# Revit family: Rundstahlbügel, Ø 21,3-219,1
name_source: partatom
category: HLS-Bauteile
revit_build: Autodesk Revit 2017 (Build: 20190507_1515(x64)
units: mm (PartAtom-declared; Revit-internal decimal feet)

## family parameters
Arbeitsebenenbasiert = Ja
Beim Laden mit Abzugskörper schneiden = Nein
Bemaßung runder Anschluss = Durchmesser verwenden
Gemeinsam genutzt = Ja
Immer vertikal = Nein
Raumberechnungspunkt = Nein
Teiletyp = Normal

## types (15) — shared parameters
Fabrikat = MEFA
Firma = MEFA Befestigungs- und Montagesysteme GmbH
Vorgabe-Ansicht = 1219 mm
zero-valued in all types: Nennweite DN Rohr, max. Profilhöhe

## per-type parameters (varying)
| type | A | Achsabstand | Artikelnummer | B | EAN | Gewicht | Gewicht pro Bauteil | Gewinde | H | Höhe | Kurztext1 | Kurztext2 | L1 | Länge Gewinde | M | Material | Materialname | Mengeneinheit | Oberflaeche | Rohraußendurchmesser | Rohraußendurchmesser Zoll | d2 | vpe |
| Rundstahlbügel, M 8, Ø 21,3 | 30 mm  [stored 0.0984252 ft] | 30 mm | 050702201 | 70 mm  [stored 0.229659 ft] |  | 0.00 kg | 0.00 kg | M8 | 85 mm  [stored 0.278871 ft] | 80 mm | Rundstahlbügel |  | 4 mm  [stored 0.0131234 ft] | 65 mm  [stored 0.213255 ft] | 8 mm  [stored 0.0262467 ft] |  |  |  |  | 21 mm | 1/2 Zoll | 7 mm  [stored 0.0229659 ft] |  |
| Rundstahlbügel, M 8, Ø 26,9 | 35 mm  [stored 0.114829 ft] | 35 mm | 050702801 | 70 mm  [stored 0.229659 ft] |  | 0.00 kg | 0.00 kg | M8 | 85 mm  [stored 0.278871 ft] | 80 mm |  |  | 1 mm  [stored 0.00328084 ft] | 65 mm  [stored 0.213255 ft] | 8 mm  [stored 0.0262467 ft] |  |  |  |  | 27 mm | 3/4 Zoll | 7 mm  [stored 0.0229659 ft] |  |
| Rundstahlbügel, M 8, Ø 33,7 | 35 mm  [stored 0.114829 ft] | 42 mm | 050703501 | 70 mm  [stored 0.229659 ft] |  | 0.00 kg | 0.00 kg | M8 | 95 mm | 90 mm |  |  | 11 mm | 65 mm  [stored 0.213255 ft] | 8 mm  [stored 0.0262467 ft] |  |  |  |  | 34 mm | 1 Zoll | 7 mm  [stored 0.0229659 ft] |  |
| Rundstahlbügel, M 8, Ø 42,4 | 51 mm | 51 mm | 050704201 | 75 mm |  | 0.00 kg | 0.00 kg | M8 | 105 mm  [stored 0.344488 ft] | 100 mm |  |  | 8 mm  [stored 0.0262467 ft] | 70 mm  [stored 0.229659 ft] | 8 mm  [stored 0.0262467 ft] |  |  |  |  | 42 mm | 1 1/4 Zoll | 7 mm  [stored 0.0229659 ft] |  |
| Rundstahlbügel, M 8, Ø 48,3 | 57 mm  [stored 0.187008 ft] | 57 mm | 050704801 | 75 mm |  | 0.00 kg | 0.00 kg | M8 | 110 mm  [stored 0.360892 ft] | 105 mm |  |  | 10 mm  [stored 0.0328084 ft] | 70 mm  [stored 0.229659 ft] | 8 mm  [stored 0.0262467 ft] |  |  |  |  | 48 mm | 1 1/2 Zoll | 7 mm  [stored 0.0229659 ft] |  |
| Rundstahlbügel, M10, Ø 60,3 | 71 mm  [stored 0.23294 ft] | 71 mm | 050706001 | 75 mm |  | 0.00 kg | 0.00 kg | M10 | 125 mm | 120 mm |  |  | 19 mm | 70 mm  [stored 0.229659 ft] | 10 mm  [stored 0.0328084 ft] |  |  |  |  | 60 mm | 2 Zoll | 9 mm |  |
| Rundstahlbügel, M10, Ø 76,1 | 87 mm  [stored 0.285433 ft] | 87 mm | 050707601 | 75 mm |  | 0.00 kg | 0.00 kg | M10 | 140 mm | 135 mm |  |  | 26 mm | 70 mm  [stored 0.229659 ft] | 10 mm  [stored 0.0328084 ft] |  |  |  |  | 76 mm | 2 1/2 Zoll | 9 mm |  |
| Rundstahlbügel, M10, Ø 88,9 | 100 mm  [stored 0.328084 ft] | 100 mm | 050708901 | 75 mm |  | 0.00 kg | 0.00 kg | M10 | 155 mm | 150 mm |  |  | 34 mm | 70 mm  [stored 0.229659 ft] | 10 mm  [stored 0.0328084 ft] |  |  |  |  | 89 mm | 3 Zoll | 9 mm |  |
| Rundstahlbügel, M12, Ø108 | 121 mm | 121 mm | 050710801 | 95 mm |  | 0.00 kg | 0.00 kg | M12 | 195 mm | 190 mm |  |  | 45 mm | 90 mm  [stored 0.295276 ft] | 12 mm  [stored 0.0393701 ft] |  |  |  |  | 108 mm  [stored 0.354331 ft] |  | 11 mm |  |
| Rundstahlbügel, M12, Ø114,3 | 126 mm | 126 mm | 050711401 | 95 mm |  | 0.00 kg | 0.00 kg | M12 | 200 mm | 195 mm |  |  | 47 mm | 90 mm  [stored 0.295276 ft] | 12 mm  [stored 0.0393701 ft] |  |  |  |  | 114 mm | 4 Zoll | 11 mm |  |
| Rundstahlbügel, M12, Ø133 | 146 mm | 146 mm | 050713301 | 95 mm |  | 0.00 kg | 0.00 kg | M12 | 220 mm | 215 mm |  |  | 57 mm  [stored 0.187008 ft] | 90 mm  [stored 0.295276 ft] | 12 mm  [stored 0.0393701 ft] |  |  |  |  | 133 mm |  | 11 mm |  |
| Rundstahlbügel, M12, Ø139,7 | 152 mm | 152 mm | 050714001 | 95 mm |  | 0.00 kg | 0.00 kg | M12 | 225 mm | 220 mm |  |  | 59 mm | 90 mm  [stored 0.295276 ft] | 12 mm  [stored 0.0393701 ft] |  |  |  |  | 140 mm | 5 Zoll | 11 mm |  |
| Rundstahlbügel, M12, Ø159 | 172 mm | 172 mm | 050715901 | 95 mm |  | 0.00 kg | 0.00 kg | M12 | 245 mm | 240 mm |  |  | 69 mm | 90 mm  [stored 0.295276 ft] | 12 mm  [stored 0.0393701 ft] |  |  |  |  | 159 mm |  | 11 mm |  |
| Rundstahlbügel, M12, Ø168,3 | 180 mm | 180 mm | 050716801 | 95 mm |  | 0.00 kg | 0.00 kg | M12 | 255 mm | 250 mm |  |  | 75 mm | 90 mm  [stored 0.295276 ft] | 12 mm  [stored 0.0393701 ft] |  |  |  |  | 168 mm | 6 Zoll | 11 mm |  |
| Rundstahlbügel, M12, Ø219,1 | 233 mm | 233 mm | 0507219 | 95 mm | 4250928414366 | 0.53 kg | 0.53 kg | M12 | 300 mm | 300 mm | Rundstahlbügel | 219.1 mm M12 Gesamthöhe 300 mm | 94 mm | 95 mm | 12 mm  [stored 0.0393701 ft] | Stahl | S235 | St | galvanisch verzinkt | 219 mm | 8 Zoll | 11 mm | 25 St |

note: [stored X ft] marks values corroborated as IEEE doubles in the binary element streams (Revit-internal decimal feet)
